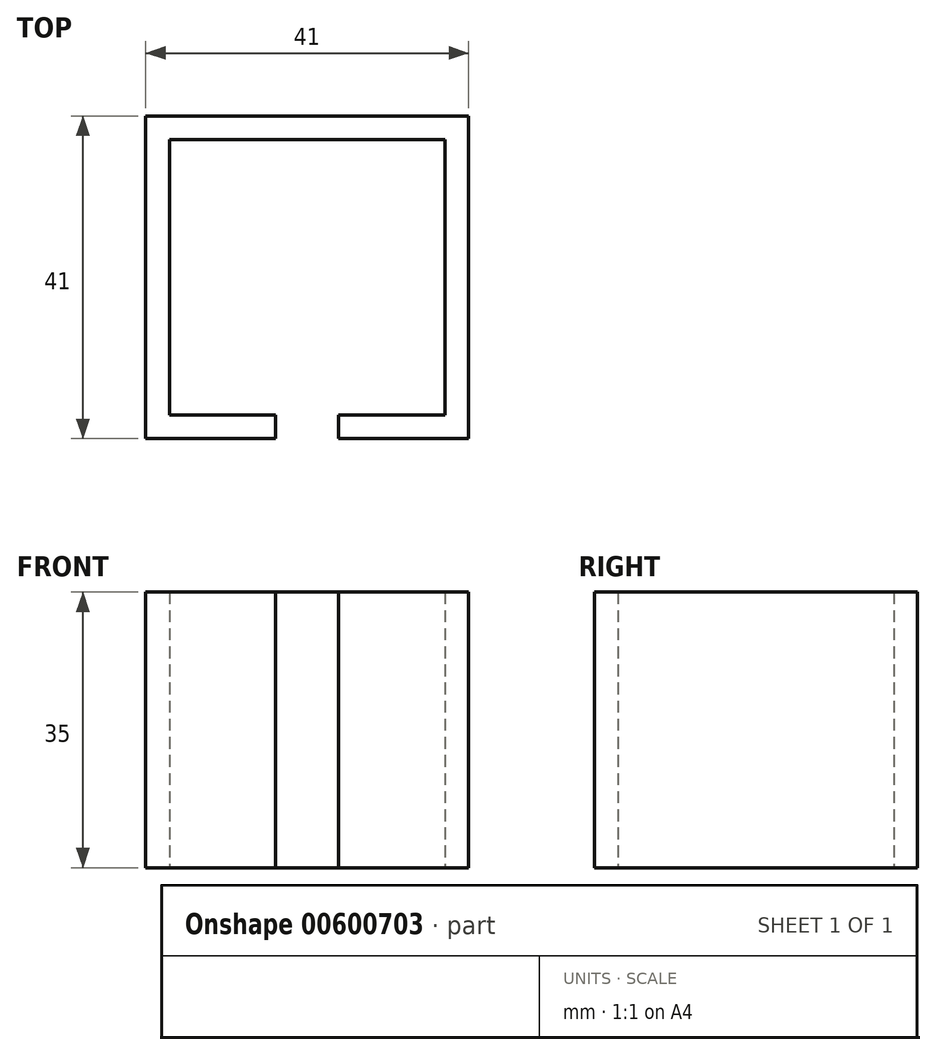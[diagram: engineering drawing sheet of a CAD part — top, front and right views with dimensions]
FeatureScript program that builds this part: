
annotation { "Feature Type Name" : "Feature", "Feature Type Description" : "" }
export const myFeature = defineFeature(function(context is Context, id is Id, definition is map)
    precondition{}
    {
        {
            var Q0;
            Q0=qCreatedBy(makeId("Top.planeOp"),FACE);
            var sketch = newSketch(context, id + "F0", { "sketchPlane" : qUnion([Q0])});
            skLineSegment(sketch, "E0.bottom", {"start": v(-17.5, 17.5) * mm, "end": v(17.5, 17.5) * mm});
            skLineSegment(sketch, "E0.top", {"start": v(-17.5, -17.5) * mm, "end": v(-4, -17.5) * mm});
            skLineSegment(sketch, "E0.left", {"start": v(-17.5, 17.5) * mm, "end": v(-17.5, -17.5) * mm});
            skLineSegment(sketch, "E0.right", {"start": v(17.5, 17.5) * mm, "end": v(17.5, -17.5) * mm});
            skPoint(sketch, "E0.middle", {"position": v(0, 0) * mm});
            skLineSegment(sketch, "E1.bottom", {"start": v(-4, -5.18) * mm, "end": v(4, -5.18) * mm});
            skLineSegment(sketch, "E1.top", {"start": v(-4, -29.82) * mm, "end": v(4, -29.82) * mm});
            skLineSegment(sketch, "E1.left", {"start": v(-4, -5.18) * mm, "end": v(-4, -29.82) * mm});
            skLineSegment(sketch, "E1.right", {"start": v(4, -5.18) * mm, "end": v(4, -29.82) * mm});
            skPoint(sketch, "E1.middle", {"position": v(0, -17.5) * mm});
            skLineSegment(sketch, "E2.0", {"start": v(20.5, 20.5) * mm, "end": v(20.5, -20.5) * mm});
            skLineSegment(sketch, "E2.1", {"start": v(-20.5, 20.5) * mm, "end": v(20.5, 20.5) * mm});
            skLineSegment(sketch, "E2.2", {"start": v(-20.5, 20.5) * mm, "end": v(-20.5, -20.5) * mm});
            skLineSegment(sketch, "E2.3", {"start": v(-20.5, -20.5) * mm, "end": v(-4, -20.5) * mm});
            skLineSegment(sketch, "E3.trimOffspring", {"start": v(4, -17.5) * mm, "end": v(17.5, -17.5) * mm});
            skLineSegment(sketch, "E4.trimOffspring", {"start": v(4, -20.5) * mm, "end": v(20.5, -20.5) * mm});
            skSolve(sketch);
        }
        {
            var Q0;
            Q0=makeQuery(id+"F0.imprint","IMPRINT",FACE,{"disambiguationData":[TD([[makeQuery(id+"F0.imprint","IMPRINT",EDGE,{"derivedFrom":sQuery(id+"F0.wireOp",EDGE,"E0.bottom")}),1.0]])]});
            extrude(context, id + "F1", {"entities" : qUnion([Q0]), "depth" : 35 * mm, "offsetDistance" : 25 * mm});
        }
    });
